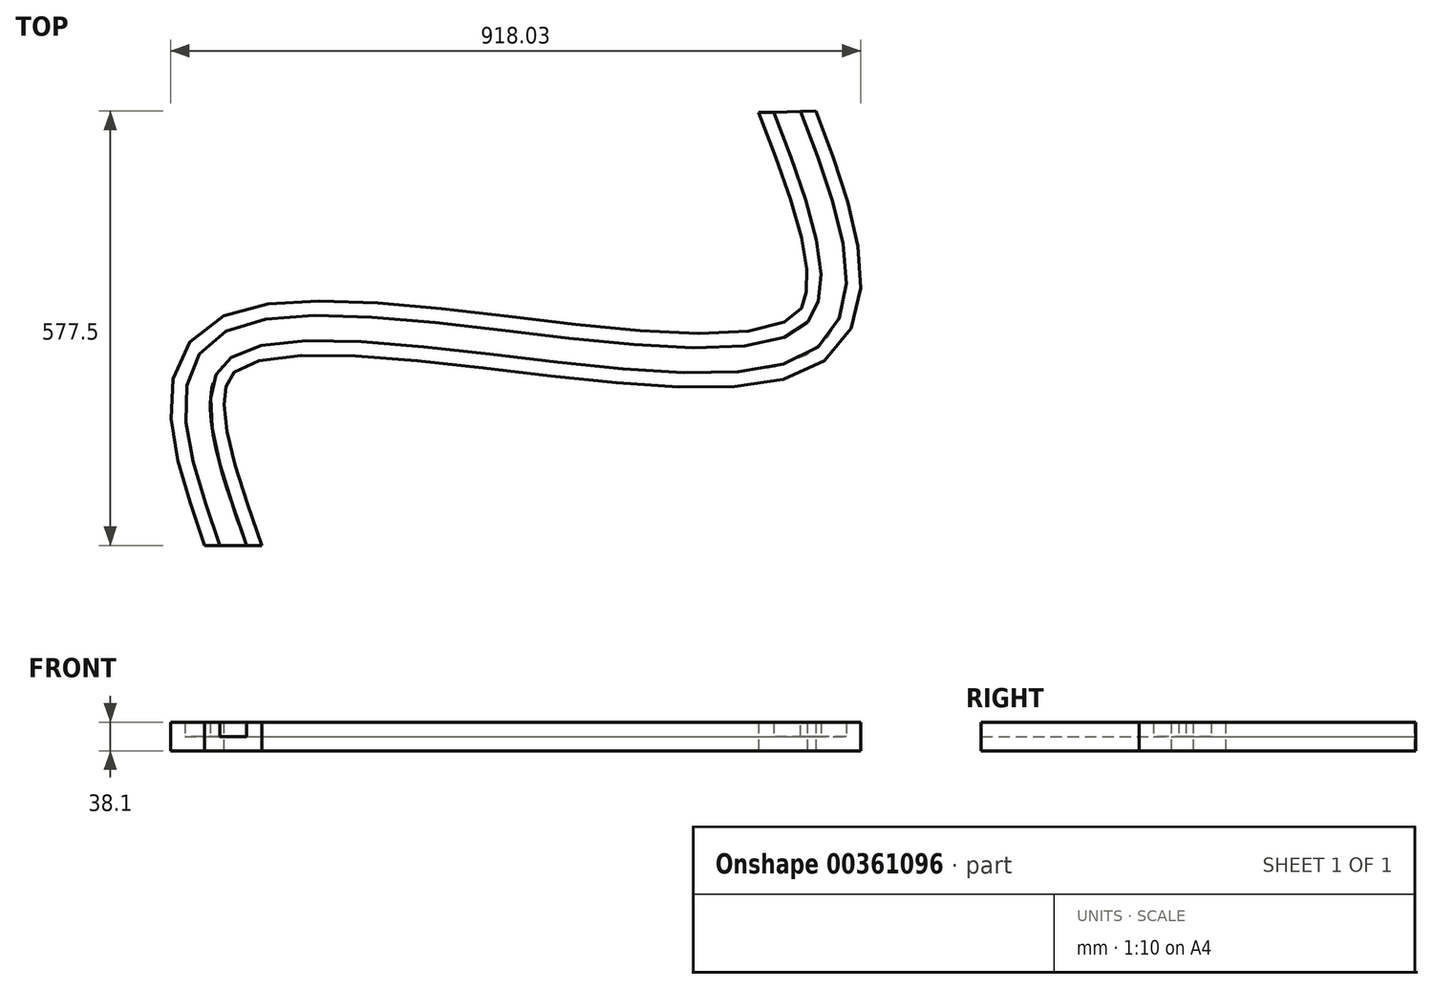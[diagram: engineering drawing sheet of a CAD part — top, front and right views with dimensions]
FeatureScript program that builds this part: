
annotation { "Feature Type Name" : "Feature", "Feature Type Description" : "" }
export const myFeature = defineFeature(function(context is Context, id is Id, definition is map)
    precondition{}
    {
        {
            var Q0;
            Q0=qCreatedBy(makeId("Front.planeOp"),FACE);
            var sketch = newSketch(context, id + "F0", { "sketchPlane" : qUnion([Q0])});
            skLineSegment(sketch, "E0.bottom", {"start": v(-38.1, 19.05) * mm, "end": v(-17.78, 19.05) * mm});
            skLineSegment(sketch, "E0.top", {"start": v(-38.1, -19.05) * mm, "end": v(38.1, -19.05) * mm});
            skLineSegment(sketch, "E0.left", {"start": v(-38.1, 19.05) * mm, "end": v(-38.1, -19.05) * mm});
            skLineSegment(sketch, "E0.right", {"start": v(38.1, 19.05) * mm, "end": v(38.1, -19.05) * mm});
            skLineSegment(sketch, "E1", {"start": v(-17.78, 19.05) * mm, "end": v(-17.78, 0) * mm});
            skLineSegment(sketch, "E2", {"start": v(-17.78, 0) * mm, "end": v(17.78, 0) * mm});
            skLineSegment(sketch, "E3", {"start": v(17.78, 0) * mm, "end": v(17.78, 19.05) * mm});
            skLineSegment(sketch, "E4.trimOffspring", {"start": v(17.78, 19.05) * mm, "end": v(38.1, 19.05) * mm});
            skSolve(sketch);
        }
        {
            var Q0;
            Q0=qCreatedBy(makeId("Top.planeOp"),FACE);
            var sketch = newSketch(context, id + "F1", { "sketchPlane" : qUnion([Q0])});
            skFitSpline(sketch, "E5", {"points": [v(0, 0) * mm, v(0, 270.7) * mm, v(749.9, 266.04) * mm, v(736.52, 576.47) * mm], "startDerivative": vector(-458.13, 1292.07) * mm, "endDerivative": vector(-534.67, 1387.94) * mm});
            skSolve(sketch);
        }
        {
            var Q0;
            Q0=makeQuery(id+"F0.imprint","IMPRINT",FACE,{"disambiguationData":[TD([[makeQuery(id+"F0.imprint","IMPRINT",EDGE,{"derivedFrom":sQuery(id+"F0.wireOp",EDGE,"E0.top")}),1.0]])]});
            var Q1;
            Q1=sQuery(id+"F1.wireOp",EDGE,"E5");
            sweep(context, id + "F2", {"profiles" : qUnion([Q0]), "path" : qUnion([Q1])});
        }
    });
